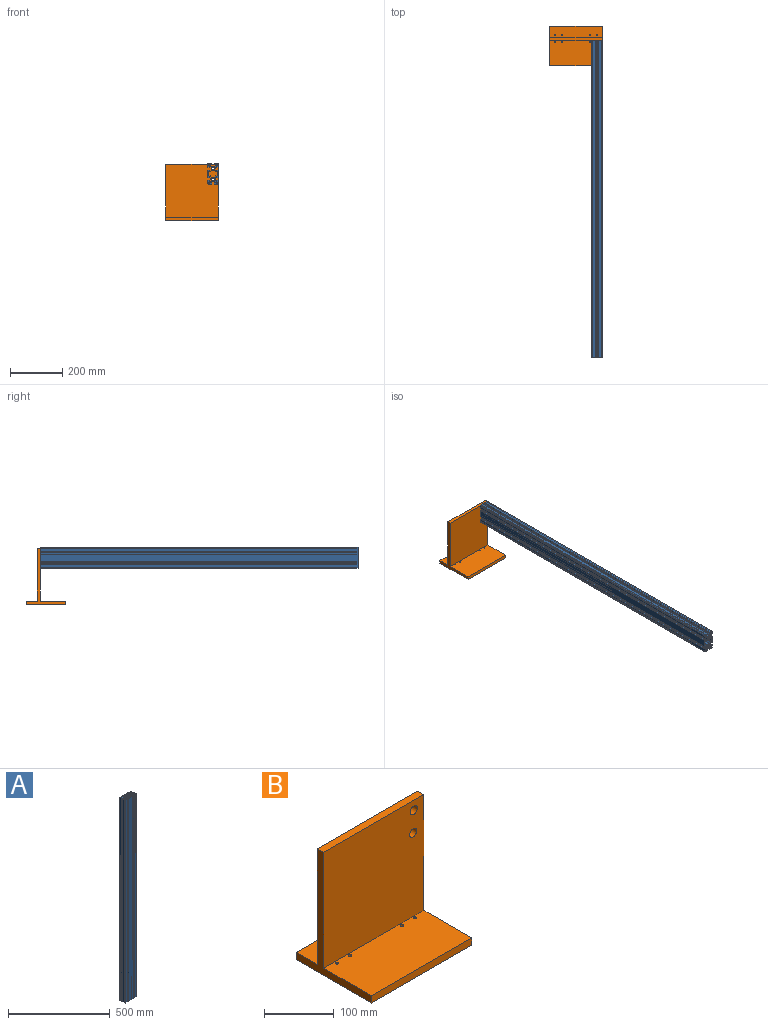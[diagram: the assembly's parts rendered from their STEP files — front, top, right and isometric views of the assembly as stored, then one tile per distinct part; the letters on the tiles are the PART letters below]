
ASSEMBLY  parts=2 mates=1
PART A: 184 faces, bbox 80x40x1219.2 mm
  f0: cylinder r=1mm len=1219.2mm, axis (0,0,-1), area 1915.1mm2, adj f1,f181,f182,f183
  f1: plane 1219.2x4mm, normal (1,0,0), area 4876.8mm2, adj f0,f2,f182,f183
  f2: cylinder r=1mm len=1219.2mm, axis (0,0,-1), area 1915.1mm2, adj f1,f3,f182,f183
  f3: plane 1219.2x4mm, normal (0,-1,0), area 4876.8mm2, adj f2,f4,f182,f183
  f4: cylinder r=1mm len=1219.2mm, axis (0,0,-1), area 1915.1mm2, adj f3,f5,f182,f183
  f5: plane 1219.2x4mm, normal (-1,0,0), area 4876.8mm2, adj f4,f6,f182,f183
  f6: cylinder r=1mm len=1219.2mm, axis (0,0,-1), area 1915.1mm2, adj f5,f181,f182,f183
  f7: plane 1219.2x2.73mm, normal (-1,0,0), area 3331.1mm2, adj f8,f174,f182,f183
  f8: plane 1219.2x5mm, normal (0,1,0), area 6096mm2, adj f7,f9,f182,f183
  f9: plane 1219.2x5.2mm, normal (-1,0,0), area 6339.8mm2, adj f8,f10,f182,f183
  f10: cylinder r=0.3mm len=1219.2mm, axis (0,0,-1), area 574.5mm2, adj f9,f11,f182,f183
  f11: plane 1219.2x11.7mm, normal (0,-1,0), area 14264.6mm2, adj f10,f12,f182,f183
  f12: cylinder r=3mm len=1219.2mm, axis (0,0,-1), area 5745.3mm2, adj f11,f13,f182,f183
  f13: plane 1219.2x11.7mm, normal (1,0,0), area 14264.6mm2, adj f12,f14,f182,f183
  f14: cylinder r=0.3mm len=1219.2mm, axis (0,0,-1), area 574.5mm2, adj f13,f15,f182,f183
  f15: plane 1219.2x5.2mm, normal (0,1,0), area 6339.8mm2, adj f14,f16,f182,f183
  f16: plane 1219.2x5mm, normal (-1,0,0), area 6096mm2, adj f15,f17,f182,f183
  f17: plane 1219.2x2.73mm, normal (0,1,0), area 3331.1mm2, adj f16,f18,f182,f183
  f18: plane 1219.2x4.27mm, normal (0.71,0.71,0), area 7358.5mm2, adj f17,f19,f182,f183
  f19: plane 1219.2x5.21mm, normal (1,0,0), area 6355.2mm2, adj f18,f20,f182,f183
  f20: plane 1219.2x0.52mm, normal (0.87,0.5,0), area 731.5mm2, adj f19,f21,f182,f183
  f21: plane 1219.2x0.52mm, normal (0.87,-0.5,0), area 731.5mm2, adj f20,f22,f182,f183
  f22: plane 1219.2x5.21mm, normal (1,0,0), area 6355.2mm2, adj f21,f23,f182,f183
  f23: plane 1219.2x4.27mm, normal (0.71,-0.71,0), area 7358.5mm2, adj f22,f24,f182,f183
  f24: plane 1219.2x2.73mm, normal (0,-1,0), area 3331.1mm2, adj f23,f25,f182,f183
  f25: plane 1219.2x5mm, normal (-1,0,0), area 6096mm2, adj f24,f26,f182,f183
  f26: plane 1219.2x5.2mm, normal (0,-1,0), area 6339.8mm2, adj f25,f27,f182,f183
  f27: cylinder r=0.3mm len=1219.2mm, axis (0,0,-1), area 574.5mm2, adj f26,f28,f182,f183
  f28: plane 1219.2x11.7mm, normal (1,0,0), area 14264.6mm2, adj f27,f29,f182,f183
  f29: cylinder r=3mm len=1219.2mm, axis (0,0,-1), area 5745.3mm2, adj f28,f30,f182,f183
  f30: plane 1219.2x11.7mm, normal (0,1,0), area 14264.6mm2, adj f29,f31,f182,f183
  f31: cylinder r=0.3mm len=1219.2mm, axis (0,0,-1), area 574.5mm2, adj f30,f32,f182,f183
  f32: plane 1219.2x5.2mm, normal (-1,0,0), area 6339.8mm2, adj f31,f33,f182,f183
  f33: plane 1219.2x5mm, normal (0,-1,0), area 6096mm2, adj f32,f34,f182,f183
  f34: plane 1219.2x2.73mm, normal (-1,0,0), area 3331.1mm2, adj f33,f35,f182,f183
  f35: plane 1219.2x4.27mm, normal (-0.71,0.71,0), area 7358.5mm2, adj f34,f36,f182,f183
  f36: plane 1219.2x5.21mm, normal (0,1,0), area 6355.2mm2, adj f35,f37,f182,f183
  f37: plane 1219.2x0.52mm, normal (-0.5,0.87,0), area 731.5mm2, adj f36,f38,f182,f183
  f38: plane 1219.2x0.52mm, normal (0.5,0.87,0), area 731.5mm2, adj f37,f39,f182,f183
  f39: plane 1219.2x5.21mm, normal (0,1,0), area 6355.2mm2, adj f38,f40,f182,f183
  f40: plane 1219.2x4.27mm, normal (0.71,0.71,0), area 7358.5mm2, adj f39,f41,f182,f183
  f41: plane 1219.2x2.73mm, normal (1,0,0), area 3331.1mm2, adj f40,f42,f182,f183
  f42: plane 1219.2x5mm, normal (0,-1,0), area 6096mm2, adj f41,f43,f182,f183
  f43: plane 1219.2x5.2mm, normal (1,0,0), area 6339.8mm2, adj f42,f44,f182,f183
  f44: cylinder r=0.3mm len=1219.2mm, axis (0,0,-1), area 574.5mm2, adj f43,f45,f182,f183
  f45: plane 1219.2x29.4mm, normal (0,1,0), area 35844.5mm2, adj f44,f46,f182,f183
  f46: cylinder r=0.3mm len=1219.2mm, axis (0,0,-1), area 574.5mm2, adj f45,f47,f182,f183
  f47: plane 1219.2x5.2mm, normal (-1,0,0), area 6339.8mm2, adj f46,f48,f182,f183
  f48: plane 1219.2x5mm, normal (0,-1,0), area 6096mm2, adj f47,f49,f182,f183
  f49: plane 1219.2x2.73mm, normal (-1,0,0), area 3331.1mm2, adj f48,f50,f182,f183
  f50: plane 1219.2x4.27mm, normal (-0.71,0.71,0), area 7358.5mm2, adj f49,f51,f182,f183
  f51: plane 1219.2x5.21mm, normal (0,1,0), area 6355.2mm2, adj f50,f52,f182,f183
  f52: plane 1219.2x0.52mm, normal (-0.5,0.87,0), area 731.5mm2, adj f51,f53,f182,f183
  f53: plane 1219.2x0.52mm, normal (0.5,0.87,0), area 731.5mm2, adj f52,f54,f182,f183
  f54: plane 1219.2x5.21mm, normal (0,1,0), area 6355.2mm2, adj f53,f55,f182,f183
  f55: plane 1219.2x4.27mm, normal (0.71,0.71,0), area 7358.5mm2, adj f54,f56,f182,f183
  f56: plane 1219.2x2.73mm, normal (1,0,0), area 3331.1mm2, adj f55,f57,f182,f183
  f57: plane 1219.2x5mm, normal (0,-1,0), area 6096mm2, adj f56,f58,f182,f183
  f58: plane 1219.2x5.2mm, normal (1,0,0), area 6339.8mm2, adj f57,f59,f182,f183
  f59: cylinder r=0.3mm len=1219.2mm, axis (0,0,-1), area 574.5mm2, adj f58,f60,f182,f183
  f60: plane 1219.2x11.7mm, normal (0,1,0), area 14264.6mm2, adj f59,f61,f182,f183
  f61: cylinder r=3mm len=1219.2mm, axis (0,0,-1), area 5745.3mm2, adj f60,f62,f182,f183
  f62: plane 1219.2x11.7mm, normal (-1,0,0), area 14264.6mm2, adj f61,f63,f182,f183
  f63: cylinder r=0.3mm len=1219.2mm, axis (0,0,-1), area 574.5mm2, adj f62,f64,f182,f183
  f64: plane 1219.2x5.2mm, normal (0,-1,0), area 6339.9mm2, adj f63,f65,f182,f183
  f65: plane 1219.2x5mm, normal (1,0,0), area 6096mm2, adj f64,f66,f182,f183
  f66: plane 1219.2x2.73mm, normal (0,-1,0), area 3331.1mm2, adj f65,f67,f182,f183
  f67: plane 1219.2x4.27mm, normal (-0.71,-0.71,0), area 7358.5mm2, adj f66,f68,f182,f183
  f68: plane 1219.2x5.21mm, normal (-1,0,0), area 6355.2mm2, adj f67,f69,f182,f183
  f69: plane 1219.2x0.52mm, normal (-0.87,-0.5,0), area 731.5mm2, adj f68,f70,f182,f183
  f70: plane 1219.2x0.52mm, normal (-0.87,0.5,0), area 731.5mm2, adj f69,f71,f182,f183
  f71: plane 1219.2x5.21mm, normal (-1,0,0), area 6355.2mm2, adj f70,f72,f182,f183
  f72: plane 1219.2x4.27mm, normal (-0.71,0.71,0), area 7358.5mm2, adj f71,f73,f182,f183
  f73: plane 1219.2x2.73mm, normal (0,1,0), area 3331.1mm2, adj f72,f74,f182,f183
  f74: plane 1219.2x5mm, normal (1,0,0), area 6096mm2, adj f73,f75,f182,f183
  f75: plane 1219.2x5.2mm, normal (0,1,0), area 6339.8mm2, adj f74,f76,f182,f183
  f76: cylinder r=0.3mm len=1219.2mm, axis (0,0,-1), area 574.5mm2, adj f75,f77,f182,f183
  f77: plane 1219.2x11.7mm, normal (-1,0,0), area 14264.6mm2, adj f76,f78,f182,f183
  f78: cylinder r=3mm len=1219.2mm, axis (0,0,-1), area 5745.3mm2, adj f77,f79,f182,f183
  f79: plane 1219.2x11.7mm, normal (0,-1,0), area 14264.6mm2, adj f78,f80,f182,f183
  f80: cylinder r=0.3mm len=1219.2mm, axis (0,0,-1), area 574.5mm2, adj f79,f81,f182,f183
  f81: plane 1219.2x5.2mm, normal (1,0,0), area 6339.8mm2, adj f80,f82,f182,f183
  f82: plane 1219.2x5mm, normal (0,1,0), area 6096mm2, adj f81,f83,f182,f183
  f83: plane 1219.2x2.73mm, normal (1,0,0), area 3331.1mm2, adj f82,f84,f182,f183
  f84: plane 1219.2x4.27mm, normal (0.71,-0.71,0), area 7358.5mm2, adj f83,f85,f182,f183
  f85: plane 1219.2x5.21mm, normal (0,-1,0), area 6355.2mm2, adj f84,f86,f182,f183
  f86: plane 1219.2x0.52mm, normal (0.5,-0.87,0), area 731.5mm2, adj f85,f87,f182,f183
  f87: plane 1219.2x0.52mm, normal (-0.5,-0.87,0), area 731.5mm2, adj f86,f88,f182,f183
  f88: plane 1219.2x5.21mm, normal (0,-1,0), area 6355.2mm2, adj f87,f89,f182,f183
  f89: plane 1219.2x4.27mm, normal (-0.71,-0.71,0), area 7358.5mm2, adj f88,f90,f182,f183
  f90: plane 1219.2x2.73mm, normal (-1,0,0), area 3331.1mm2, adj f89,f91,f182,f183
  f91: plane 1219.2x5mm, normal (0,1,0), area 6096mm2, adj f90,f92,f182,f183
  f92: plane 1219.2x5.2mm, normal (-1,0,0), area 6339.8mm2, adj f91,f93,f182,f183
  f93: cylinder r=0.3mm len=1219.2mm, axis (0,0,-1), area 574.5mm2, adj f92,f94,f182,f183
  f94: plane 1219.2x29.4mm, normal (0,-1,0), area 35844.5mm2, adj f93,f95,f182,f183
  f95: cylinder r=0.3mm len=1219.2mm, axis (0,0,-1), area 574.5mm2, adj f94,f96,f182,f183
  f96: plane 1219.2x5.2mm, normal (1,0,0), area 6339.8mm2, adj f95,f97,f182,f183
  f97: plane 1219.2x5mm, normal (0,1,0), area 6096mm2, adj f96,f98,f182,f183
  f98: plane 1219.2x2.73mm, normal (1,0,0), area 3331.1mm2, adj f97,f99,f182,f183
  f99: plane 1219.2x4.27mm, normal (0.71,-0.71,0), area 7358.5mm2, adj f98,f100,f182,f183
  f100: plane 1219.2x5.21mm, normal (0,-1,0), area 6355.2mm2, adj f99,f101,f182,f183
  f101: plane 1219.2x0.52mm, normal (0.5,-0.87,0), area 731.5mm2, adj f100,f102,f182,f183
  f102: plane 1219.2x0.52mm, normal (-0.5,-0.87,0), area 731.5mm2, adj f101,f103,f182,f183
  f103: plane 1219.2x5.21mm, normal (0,-1,0), area 6355.2mm2, adj f102,f174,f182,f183
  f104: cylinder r=1mm len=1219.2mm, axis (0,0,-1), area 1915.1mm2, adj f105,f175,f182,f183
  f105: plane 1219.2x13mm, normal (0,1,0), area 15849.6mm2, adj f104,f106,f182,f183
  f106: cylinder r=1mm len=1219.2mm, axis (0,0,-1), area 1915.1mm2, adj f105,f107,f182,f183
  f107: plane 1219.2x4.85mm, normal (1,0,0), area 5917.5mm2, adj f106,f108,f182,f183
  f108: cylinder r=1mm len=1219.2mm, axis (0,0,-1), area 957.6mm2, adj f107,f109,f182,f183
  f109: plane 1219.2x4.71mm, normal (0.71,0.71,0), area 8116mm2, adj f108,f110,f182,f183
  f110: plane 1219.2x11.46mm, normal (1,0,0), area 13977.5mm2, adj f109,f111,f182,f183
  f111: plane 1219.2x4.71mm, normal (0.71,-0.71,0), area 8116mm2, adj f110,f112,f182,f183
  f112: cylinder r=1mm len=1219.2mm, axis (0,0,-1), area 957.6mm2, adj f111,f113,f182,f183
  f113: plane 1219.2x4.85mm, normal (1,0,0), area 5917.5mm2, adj f112,f114,f182,f183
  f114: cylinder r=1mm len=1219.2mm, axis (0,0,-1), area 1915.1mm2, adj f113,f115,f182,f183
  f115: plane 1219.2x13mm, normal (0,-1,0), area 15849.6mm2, adj f114,f116,f182,f183
  f116: cylinder r=1mm len=1219.2mm, axis (0,0,-1), area 1915.1mm2, adj f115,f117,f182,f183
  f117: plane 1219.2x4.85mm, normal (-1,0,0), area 5917.4mm2, adj f116,f118,f182,f183
  f118: cylinder r=1mm len=1219.2mm, axis (0,0,-1), area 957.6mm2, adj f117,f119,f182,f183
  f119: plane 1219.2x4.71mm, normal (-0.71,-0.71,0), area 8116mm2, adj f118,f120,f182,f183
  f120: plane 1219.2x11.46mm, normal (-1,0,0), area 13977.5mm2, adj f119,f121,f182,f183
  f121: plane 1219.2x4.71mm, normal (-0.71,0.71,0), area 8116mm2, adj f120,f122,f182,f183
  f122: cylinder r=1mm len=1219.2mm, axis (0,0,-1), area 957.6mm2, adj f121,f175,f182,f183
  f123: cylinder r=1mm len=1219.2mm, axis (0,0,-1), area 1915.1mm2, adj f124,f176,f182,f183
  f124: plane 1219.2x4mm, normal (1,0,0), area 4876.8mm2, adj f123,f125,f182,f183
  f125: cylinder r=1mm len=1219.2mm, axis (0,0,-1), area 1915.1mm2, adj f124,f126,f182,f183
  f126: plane 1219.2x4mm, normal (0,-1,0), area 4876.8mm2, adj f125,f127,f182,f183
  f127: cylinder r=1mm len=1219.2mm, axis (0,0,-1), area 1915.1mm2, adj f126,f128,f182,f183
  f128: plane 1219.2x4mm, normal (-1,0,0), area 4876.8mm2, adj f127,f129,f182,f183
  f129: cylinder r=1mm len=1219.2mm, axis (0,0,-1), area 1915.1mm2, adj f128,f176,f182,f183
  f130: cylinder r=5.25mm len=1219.2mm, axis (0,0,-1), area 7796.4mm2, adj f131,f177,f182,f183
  f131: cylinder r=0.38mm len=1219.2mm, axis (0,0,-1), area 984.5mm2, adj f130,f132,f182,f183
  f132: cylinder r=1mm len=1219.2mm, axis (0,0,-1), area 5721.6mm2, adj f131,f133,f182,f183
  f133: cylinder r=0.38mm len=1219.2mm, axis (0,0,-1), area 983.4mm2, adj f132,f134,f182,f183
  f134: cylinder r=5.25mm len=1219.2mm, axis (0,0,-1), area 7795.2mm2, adj f133,f135,f182,f183
  f135: cylinder r=0.38mm len=1219.2mm, axis (0,0,-1), area 986.2mm2, adj f134,f136,f182,f183
  f136: cylinder r=1mm len=1219.2mm, axis (0,0,-1), area 5721.6mm2, adj f135,f137,f182,f183
  f137: cylinder r=0.38mm len=1219.2mm, axis (0,0,-1), area 984.3mm2, adj f136,f138,f182,f183
  f138: cylinder r=5.25mm len=1219.2mm, axis (0,0,-1), area 7796.8mm2, adj f137,f139,f182,f183
  f139: cylinder r=0.38mm len=1219.2mm, axis (0,0,-1), area 983.7mm2, adj f138,f140,f182,f183
  f140: cylinder r=1mm len=1219.2mm, axis (0,0,-1), area 5722.1mm2, adj f139,f141,f182,f183
  f141: cylinder r=0.38mm len=1219.2mm, axis (0,0,-1), area 984.4mm2, adj f140,f142,f182,f183
  f142: cylinder r=5.25mm len=1219.2mm, axis (0,0,-1), area 7796.2mm2, adj f141,f143,f182,f183
  f143: cylinder r=0.38mm len=1219.2mm, axis (0,0,-1), area 985mm2, adj f142,f144,f182,f183
  f144: cylinder r=1mm len=1219.2mm, axis (0,0,-1), area 5718.4mm2, adj f143,f177,f182,f183
  f145: cylinder r=1mm len=1219.2mm, axis (0,0,-1), area 1915.1mm2, adj f146,f178,f182,f183
  f146: plane 1219.2x4mm, normal (1,0,0), area 4876.8mm2, adj f145,f147,f182,f183
  f147: cylinder r=1mm len=1219.2mm, axis (0,0,-1), area 1915.1mm2, adj f146,f148,f182,f183
  f148: plane 1219.2x4mm, normal (0,-1,0), area 4876.8mm2, adj f147,f149,f182,f183
  f149: cylinder r=1mm len=1219.2mm, axis (0,0,-1), area 1915.1mm2, adj f148,f150,f182,f183
  f150: plane 1219.2x4mm, normal (-1,0,0), area 4876.8mm2, adj f149,f151,f182,f183
  f151: cylinder r=1mm len=1219.2mm, axis (0,0,-1), area 1915.1mm2, adj f150,f178,f182,f183
  f152: plane 1219.2x4mm, normal (0,1,0), area 4876.8mm2, adj f153,f179,f182,f183
  f153: cylinder r=1mm len=1219.2mm, axis (0,0,-1), area 1915.1mm2, adj f152,f154,f182,f183
  f154: plane 1219.2x4mm, normal (1,0,0), area 4876.8mm2, adj f153,f155,f182,f183
  f155: cylinder r=1mm len=1219.2mm, axis (0,0,-1), area 1915.1mm2, adj f154,f156,f182,f183
  f156: plane 1219.2x4mm, normal (0,-1,0), area 4876.8mm2, adj f155,f157,f182,f183
  f157: cylinder r=1mm len=1219.2mm, axis (0,0,-1), area 1915.1mm2, adj f156,f158,f182,f183
  f158: plane 1219.2x4mm, normal (-1,0,0), area 4876.8mm2, adj f157,f179,f182,f183
  f159: cylinder r=5.25mm len=1219.2mm, axis (0,0,-1), area 7796.4mm2, adj f160,f180,f182,f183
  f160: cylinder r=0.38mm len=1219.2mm, axis (0,0,-1), area 984.5mm2, adj f159,f161,f182,f183
  f161: cylinder r=1mm len=1219.2mm, axis (0,0,-1), area 5721.6mm2, adj f160,f162,f182,f183
  f162: cylinder r=0.38mm len=1219.2mm, axis (0,0,-1), area 983.4mm2, adj f161,f163,f182,f183
  f163: cylinder r=5.25mm len=1219.2mm, axis (0,0,-1), area 7795.2mm2, adj f162,f164,f182,f183
  f164: cylinder r=0.38mm len=1219.2mm, axis (0,0,-1), area 986.2mm2, adj f163,f165,f182,f183
  f165: cylinder r=1mm len=1219.2mm, axis (0,0,-1), area 5721.6mm2, adj f164,f166,f182,f183
  f166: cylinder r=0.38mm len=1219.2mm, axis (0,0,-1), area 984.3mm2, adj f165,f167,f182,f183
  f167: cylinder r=5.25mm len=1219.2mm, axis (0,0,-1), area 7796.8mm2, adj f166,f168,f182,f183
  f168: cylinder r=0.38mm len=1219.2mm, axis (0,0,-1), area 983.7mm2, adj f167,f169,f182,f183
  f169: cylinder r=1mm len=1219.2mm, axis (0,0,-1), area 5722.1mm2, adj f168,f170,f182,f183
  f170: cylinder r=0.38mm len=1219.2mm, axis (0,0,-1), area 984.4mm2, adj f169,f171,f182,f183
  f171: cylinder r=5.25mm len=1219.2mm, axis (0,0,-1), area 7796.2mm2, adj f170,f172,f182,f183
  f172: cylinder r=0.38mm len=1219.2mm, axis (0,0,-1), area 985mm2, adj f171,f173,f182,f183
  f173: cylinder r=1mm len=1219.2mm, axis (0,0,-1), area 5718.4mm2, adj f172,f180,f182,f183
  f174: plane 1219.2x4.27mm, normal (-0.71,-0.71,0), area 7358.5mm2, adj f7,f103,f182,f183
  f175: plane 1219.2x4.85mm, normal (-1,0,0), area 5917.4mm2, adj f104,f122,f182,f183
  f176: plane 1219.2x4mm, normal (0,1,0), area 4876.8mm2, adj f123,f129,f182,f183
  f177: cylinder r=0.38mm len=1219.2mm, axis (0,0,-1), area 986.7mm2, adj f130,f144,f182,f183
  f178: plane 1219.2x4mm, normal (0,1,0), area 4876.8mm2, adj f145,f151,f182,f183
  f179: cylinder r=1mm len=1219.2mm, axis (0,0,-1), area 1915.1mm2, adj f152,f158,f182,f183
  f180: cylinder r=0.38mm len=1219.2mm, axis (0,0,-1), area 986.7mm2, adj f159,f173,f182,f183
  f181: plane 1219.2x4mm, normal (0,1,0), area 4876.8mm2, adj f0,f6,f182,f183
  f182: plane 80x40mm, normal (0,0,1), area 1114mm2, adj f0,f1,f2,f3,f4,f5,f6,f7
  f183: plane 80x40mm, normal (0,0,-1), area 1114mm2, adj f0,f1,f2,f3,f4,f5,f6,f7
PART B: 20 faces, bbox 203.2x152.4x215.9 mm
  f0: plane 203.2x96.77mm, normal (0,0,1), area 19592.1mm2, adj f2,f3,f4,f9,f10,f13,f14,f16
  f1: plane 203.2x12.7mm, normal (0,1,0), area 2580.6mm2, adj f2,f4,f5,f6
  f2: plane 215.9x152.4mm, normal (-1,0,0), area 4516.1mm2, adj f0,f1,f3,f5,f6,f15,f16,f17
  f3: plane 203.2x12.7mm, normal (0,-1,0), area 2580.6mm2, adj f0,f2,f4,f6
  f4: plane 215.9x152.4mm, normal (1,0,0), area 4516.1mm2, adj f0,f1,f3,f5,f6,f15,f16,f17
  f5: plane 203.2x42.93mm, normal (0,0,1), area 8650.2mm2, adj f1,f2,f4,f7,f8,f11,f12,f17
  f6: plane 203.2x152.4mm, normal (0,0,-1), area 30822.9mm2, adj f1,f2,f3,f4,f7,f8,f9,f10
  f7: cylinder r=2.4mm len=12.7mm, axis (0,0,-1), area 191.5mm2, adj f5,f6
  f8: cylinder r=2.4mm len=12.7mm, axis (0,0,-1), area 191.5mm2, adj f5,f6
  f9: cylinder r=2.4mm len=12.7mm, axis (0,0,-1), area 191.5mm2, adj f0,f6
  f10: cylinder r=2.4mm len=12.7mm, axis (0,0,-1), area 191.5mm2, adj f0,f6
  f11: cylinder r=2.4mm len=12.7mm, axis (0,0,-1), area 191.5mm2, adj f5,f6
  f12: cylinder r=2.4mm len=12.7mm, axis (0,0,-1), area 191.5mm2, adj f5,f6
  f13: cylinder r=2.4mm len=12.7mm, axis (0,0,-1), area 191.5mm2, adj f0,f6
  f14: cylinder r=2.4mm len=12.7mm, axis (0,0,-1), area 191.5mm2, adj f0,f6
  f15: plane 203.2x12.7mm, normal (0,0,1), area 2580.6mm2, adj f2,f4,f16,f17
  f16: plane 203.2x203.2mm, normal (0,-1,0), area 40960mm2, adj f0,f2,f4,f15,f18,f19
  f17: plane 203.2x203.2mm, normal (0,1,0), area 40960mm2, adj f2,f4,f5,f15,f18,f19
  f18: cylinder r=7.25mm len=14.5mm, axis (0,-1,0), area 578.5mm2, adj f16,f17
  f19: cylinder r=7.25mm len=14.5mm, axis (0,-1,0), area 578.5mm2, adj f16,f17
PLACE A rot(axis=(-0.58,-0.58,-0.58),120deg) t=(80.93,-1198.63,178.88)mm
PLACE B at identity
MATE fastened A.f159 <-> B.f19  axis (0,-1,0) through (80.93,20.57,198.88)mm
